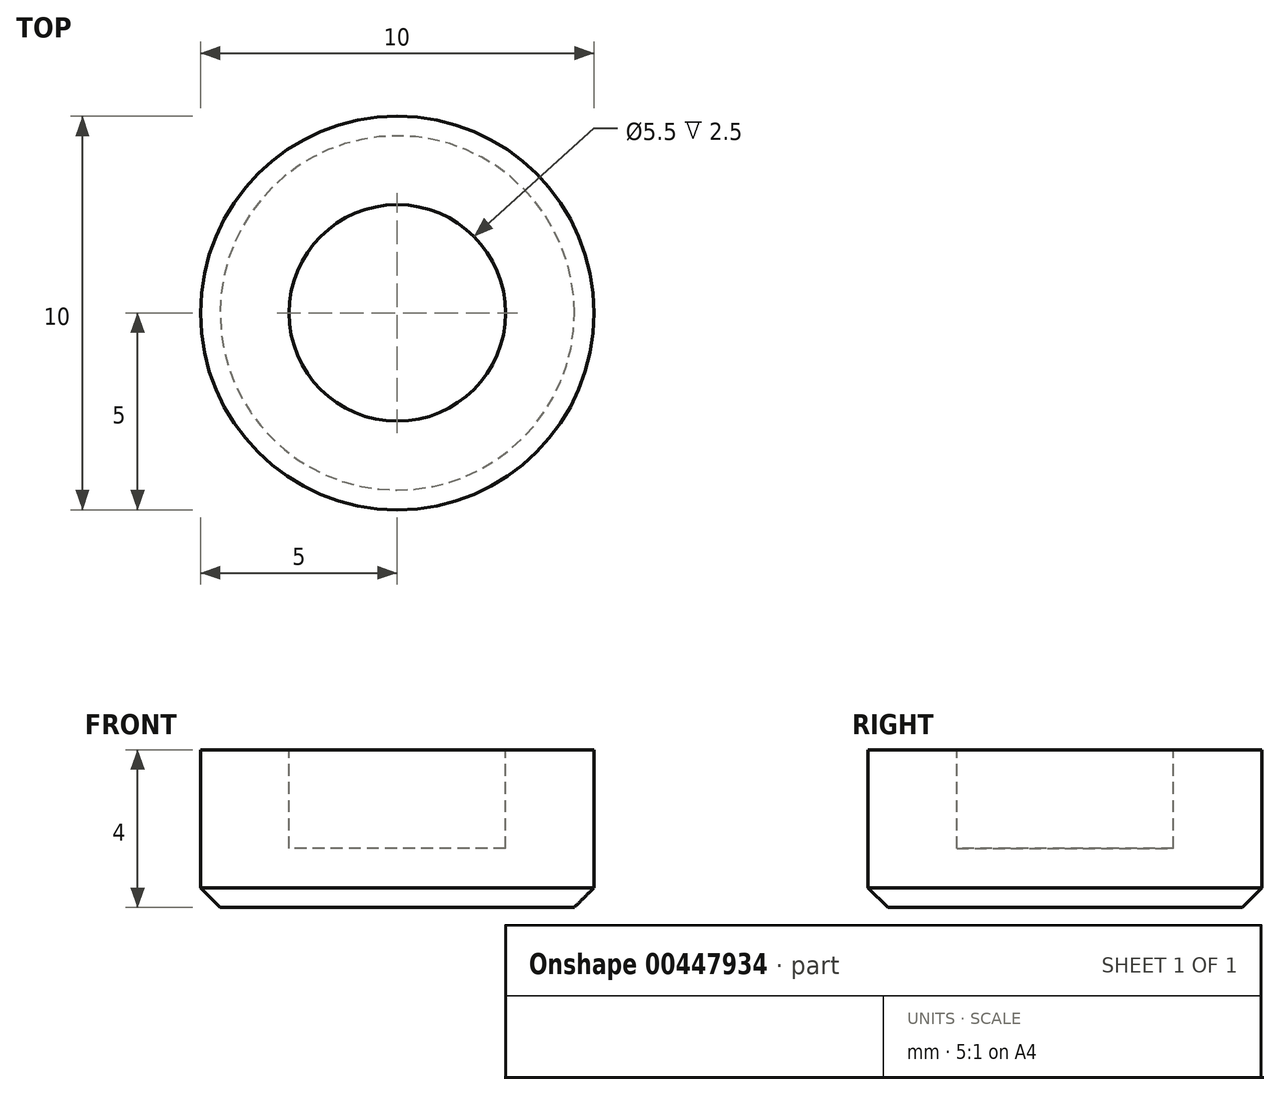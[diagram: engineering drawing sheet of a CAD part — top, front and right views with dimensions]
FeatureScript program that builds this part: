
annotation { "Feature Type Name" : "Feature", "Feature Type Description" : "" }
export const myFeature = defineFeature(function(context is Context, id is Id, definition is map)
    precondition{}
    {
        {
            var Q0;
            Q0=qCreatedBy(makeId("Top.planeOp"),FACE);
            var sketch = newSketch(context, id + "F0", { "sketchPlane" : qUnion([Q0])});
            skCircle(sketch, "E0", {"center": v(0, 0) * mm, "radius": 5 * mm});
            skSolve(sketch);
        }
        {
            var Q0;
            Q0 = qSketchRegion(id + "F0", true);
            extrude(context, id + "F1", {"entities" : qUnion([Q0]), "depth" : 4 * mm});
        }
        {
            var Q0;
            Q0=makeQuery(id+"F1.opExtrude","CAP_FACE",FACE,{"disambiguationData":[OSD([sQuery(id+"F0.wireOp",EDGE,"E0")])],"isStart":false});
            var sketch = newSketch(context, id + "F2", { "sketchPlane" : qUnion([Q0])});
            skCircle(sketch, "E1", {"center": v(0, 0) * mm, "radius": 2.75 * mm});
            skSolve(sketch);
        }
        {
            var Q0;
            Q0 = qSketchRegion(id + "F2", true);
            extrude(context, id + "F3", {"entities" : qUnion([Q0]), "operationType" : NewBodyOperationType.REMOVE, "oppositeDirection" : true, "depth" : 2.5 * mm});
        }
        {
            var Q0;
            Q0=makeQuery(id+"F3.boolean.opBoolean","COPY",EDGE,{"derivedFrom":makeQuery(id+"F3.opExtrude","CAP_EDGE",EDGE,{"disambiguationData":[OSD([sQuery(id+"F2.wireOp",EDGE,"E1")])],"isStart":true})});
            var Q1;
            Q1=makeQuery(id+"F1.opExtrude","CAP_EDGE",EDGE,{"disambiguationData":[OSD([sQuery(id+"F0.wireOp",EDGE,"E0")])],"isStart":true});
            chamfer(context, id + "F4", {"entities" : qUnion([Q0, Q1]), "width" : .5 * mm, "tangentPropagation" : true});
        }
    });
